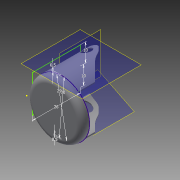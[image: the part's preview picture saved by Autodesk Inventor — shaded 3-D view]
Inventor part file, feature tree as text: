
AUTODESK INVENTOR PART (.ipt)
format: ipt  version: 2014 (Build 180170000, 170)  size: 218,624 bytes
history: native  units: mm
features: fillet x7, sketch x5, chamfer x4, extrude x3, plane x3, hole x2, shell x1
ambient origin geometry x8: Origin, YZ Plane, XZ Plane, XY Plane, X Axis, Y Axis, Z Axis, Center Point
bodies: Solid1 (feature_tree)
feature tree (25):
  extrude  "Extrusion1"  Depth=4.0mm TaperAngle=0.0deg
  shell  "Shell1"  Thickness=1.0mm
  sketch  "Sketch2"  dims[d4=29.0mm d5=30.0mm d8=26.0mm]
  plane  "Work Plane1"
  sketch  "Sketch4"  dims[d9=10.0mm d10=10.0mm]
  extrude  "Extrusion4"  Depth=30.0mm
  fillet  "Fillet1"  Radius=26.0mm
  extrude  "Extrusion5"  Depth=10.0mm
  chamfer  "Chamfer1"  Distance=25.0mm
  chamfer  "Chamfer2"  Distance=3.0mm
  chamfer  "Chamfer3"  Distance=18.0mm
  fillet  "Fillet2"  Radius=9.0mm
  chamfer  "Chamfer4"  Distance=9.0mm Angle=45.0deg
  fillet  "Fillet3"  Radius=5.0mm
  fillet  "Fillet4"  Radius=9.0mm
  fillet  "Fillet5"  Radius=5.0mm
  fillet  "Fillet6"  Radius=9.0mm
  fillet  "Fillet7"  Radius=4.0mm
  plane  "Work Plane3"
  hole  "Hole1"  [1 undecoded]
  plane  "Work Plane4"
  hole  "Hole2"  [1 undecoded]
  sketch  "Sketch1"  dims[d0=30.0mm d1=4.0mm d2=0.0mm d3=1.0mm]
  sketch  "Sketch6"  dims[d11=0.5mm]
  sketch  "Sketch7"  dims[d12=0.5mm d15=25.0mm d16=0.0mm d17=3.0mm d19=18.0mm d20=0.0mm d21=9.0mm d22=2.0mm d23=45.0deg d24=9.0mm d25=2.0mm d26=45.0deg d27=5.0mm d28=2.0mm d29=45.0deg d30=9.0mm d31=5.0mm d32=2.0mm d33=45.0deg d34=9.0mm d35=4.0mm d36=4.0mm d37=15.0mm d38=15.0mm d42=5.0mm d43=5.0mm d44=5.0mm d45=6.0mm d46=4.0mm d47=2.0mm d48=90.0deg d49=8.0mm d50=20.594885mm d51=5.0mm d52=5.0mm d53=5.0mm d54=6.0mm d55=4.0mm d56=2.0mm d57=90.0deg d58=8.0mm d59=20.594885mm]
note: 2 required parameter values undecoded (feature->parameter linkage not recoverable at this tier; creation-order binding heuristic only, values carry confidence <= 0.55)
